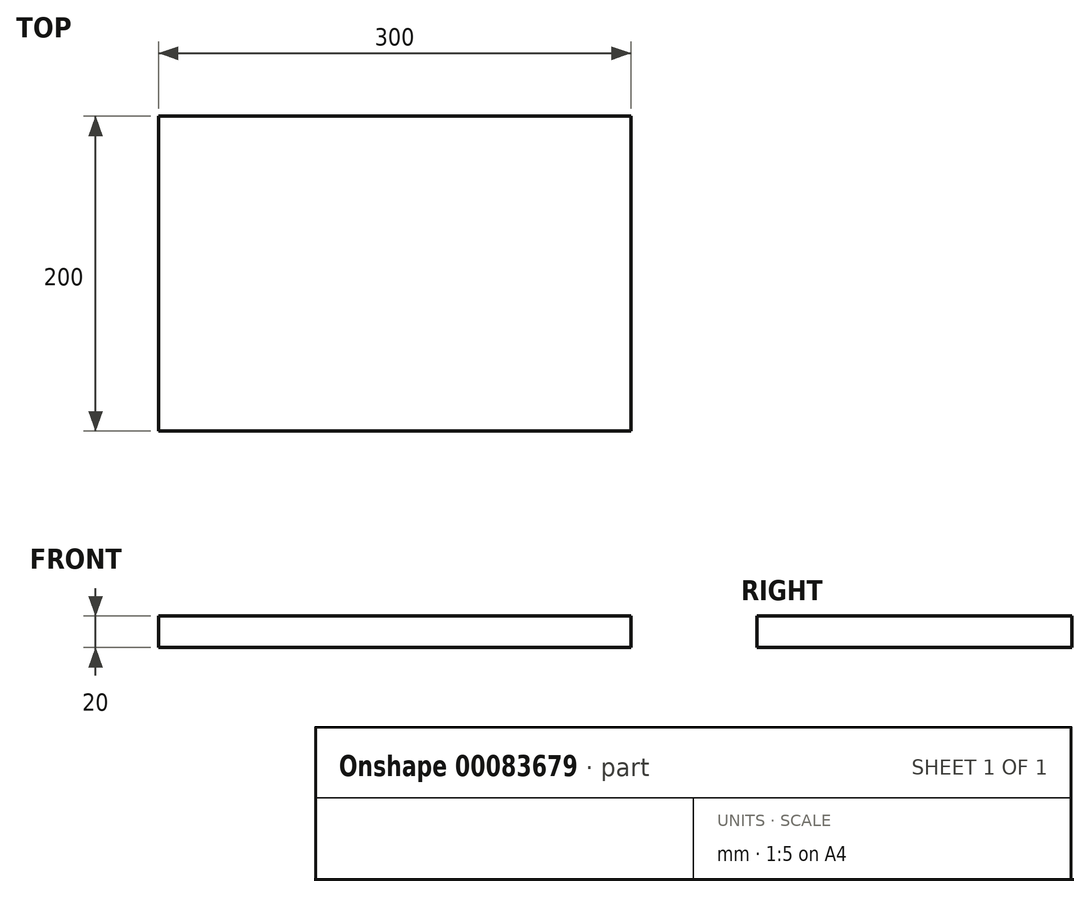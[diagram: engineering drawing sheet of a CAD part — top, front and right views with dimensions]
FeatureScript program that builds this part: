
annotation { "Feature Type Name" : "Feature", "Feature Type Description" : "" }
export const myFeature = defineFeature(function(context is Context, id is Id, definition is map)
    precondition{}
    {
        {
            var Q0;
            Q0=qCreatedBy(makeId("Top.planeOp"),FACE);
            var sketch = newSketch(context, id + "F0", { "sketchPlane" : qUnion([Q0])});
            skLineSegment(sketch, "E0.bottom", {"start": v(100, -100) * mm, "end": v(400, -100) * mm});
            skLineSegment(sketch, "E0.top", {"start": v(100, -300) * mm, "end": v(400, -300) * mm});
            skLineSegment(sketch, "E0.left", {"start": v(100, -100) * mm, "end": v(100, -300) * mm});
            skLineSegment(sketch, "E0.right", {"start": v(400, -100) * mm, "end": v(400, -300) * mm});
            skLineSegment(sketch, "E1", {"start": v(400, -100) * mm, "end": v(400, 0) * mm, "construction": true});
            skLineSegment(sketch, "E2", {"start": v(100, -100) * mm, "end": v(100, 0) * mm, "construction": true});
            skLineSegment(sketch, "E3", {"start": v(100, -100) * mm, "end": v(0, -100) * mm, "construction": true});
            skLineSegment(sketch, "E4", {"start": v(100, -300) * mm, "end": v(0, -300) * mm, "construction": true});
            skSolve(sketch);
        }
        {
            var Q0;
            Q0=qCreatedBy(makeId("Right.planeOp"),FACE);
            var sketch = newSketch(context, id + "F1", { "sketchPlane" : qUnion([Q0])});
            skLineSegment(sketch, "E5.bottom", {"start": v(-300, 100) * mm, "end": v(-100, 100) * mm});
            skLineSegment(sketch, "E5.top", {"start": v(-300, 120) * mm, "end": v(-100, 120) * mm});
            skLineSegment(sketch, "E5.left", {"start": v(-300, 100) * mm, "end": v(-300, 120) * mm});
            skLineSegment(sketch, "E5.right", {"start": v(-100, 100) * mm, "end": v(-100, 120) * mm});
            skLineSegment(sketch, "E6", {"start": v(-100, 120) * mm, "end": v(0, 120) * mm, "construction": true});
            skLineSegment(sketch, "E7", {"start": v(-100, 100) * mm, "end": v(0, 100) * mm, "construction": true});
            skSolve(sketch);
        }
        {
            var Q0;
            Q0=qCreatedBy(makeId("Front.planeOp"),FACE);
            var sketch = newSketch(context, id + "F2", { "sketchPlane" : qUnion([Q0])});
            skLineSegment(sketch, "E8.bottom", {"start": v(100, 120) * mm, "end": v(400, 120) * mm});
            skLineSegment(sketch, "E8.top", {"start": v(100, 100) * mm, "end": v(400, 100) * mm});
            skLineSegment(sketch, "E8.left", {"start": v(100, 120) * mm, "end": v(100, 100) * mm});
            skLineSegment(sketch, "E8.right", {"start": v(400, 120) * mm, "end": v(400, 100) * mm});
            skSolve(sketch);
        }
        {
            var Q0;
            Q0=makeQuery(id+"F0.imprint","IMPRINT",FACE,{"disambiguationData":[TD([[makeQuery(id+"F0.imprint","IMPRINT",EDGE,{"derivedFrom":sQuery(id+"F0.wireOp",EDGE,"E0.bottom")}),-1.0]])]});
            extrude(context, id + "F3", {"entities" : qUnion([Q0]), "depth" : 10000 * mm});
        }
        {
            var Q0;
            Q0=makeQuery(id+"F2.imprint","IMPRINT",FACE,{"disambiguationData":[TD([[makeQuery(id+"F2.imprint","IMPRINT",EDGE,{"derivedFrom":sQuery(id+"F2.wireOp",EDGE,"E8.bottom")}),-1.0]])]});
            extrude(context, id + "F4", {"entities" : qUnion([Q0]), "operationType" : NewBodyOperationType.INTERSECT, "endBound" : BoundingType.THROUGH_ALL, "depth" : 25 * mm, "hasSecondDirection" : true, "secondDirectionBound" : BoundingType.THROUGH_ALL, "secondDirectionOppositeDirection" : true, "secondDirectionDepth" : 25 * mm});
        }
    });
